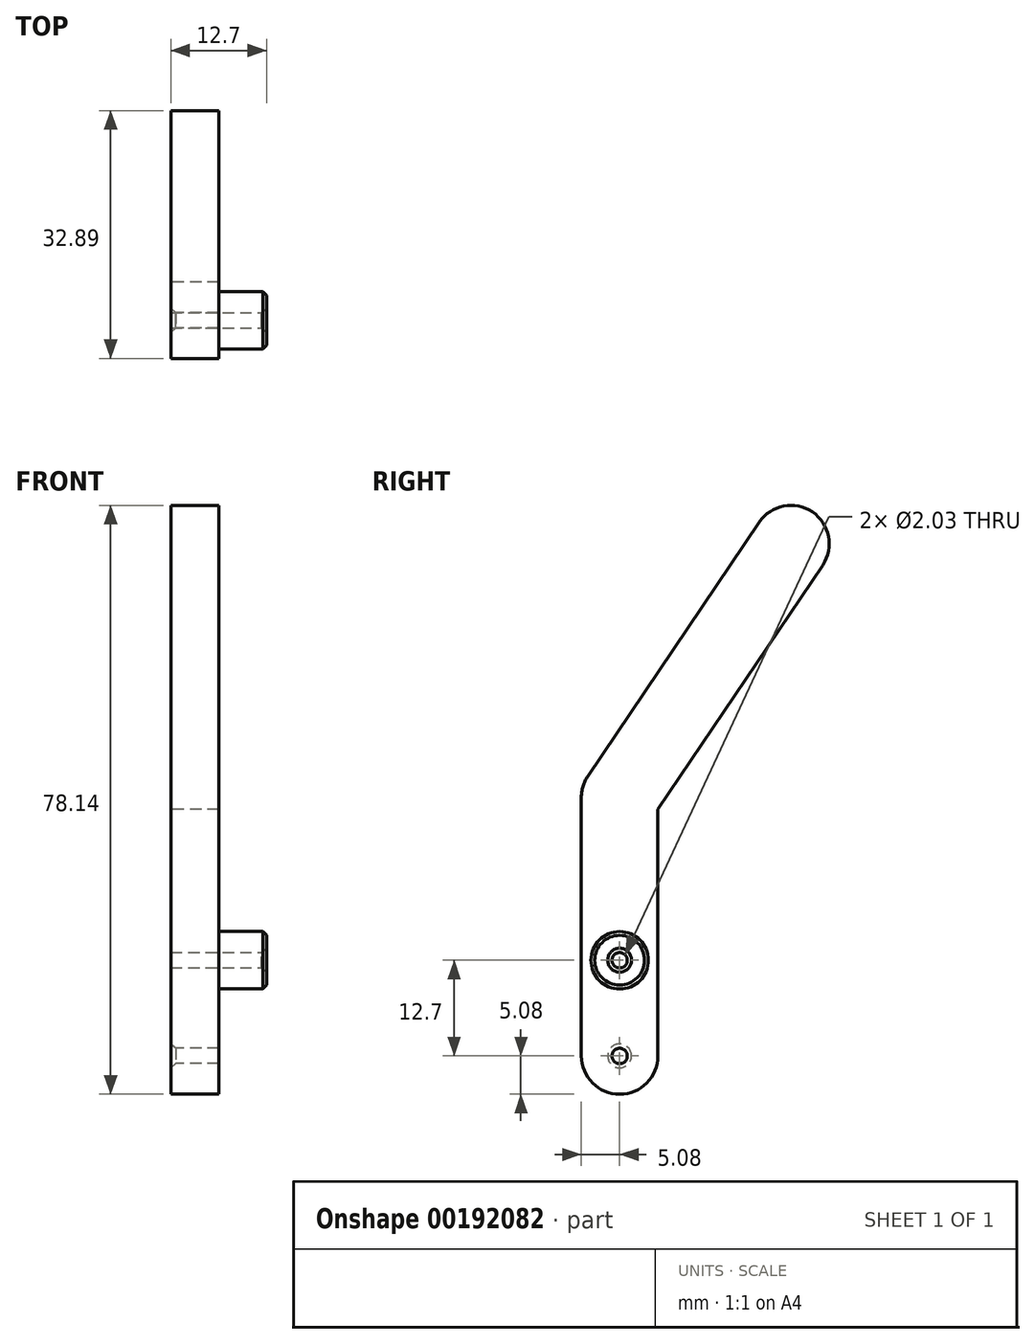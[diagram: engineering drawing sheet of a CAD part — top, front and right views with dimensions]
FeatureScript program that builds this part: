
annotation { "Feature Type Name" : "Feature", "Feature Type Description" : "" }
export const myFeature = defineFeature(function(context is Context, id is Id, definition is map)
    precondition{}
    {
        {
            var Q0;
            Q0=qCreatedBy(makeId("Right.planeOp"),FACE);
            var sketch = newSketch(context, id + "F0", { "sketchPlane" : qUnion([Q0])});
            skLineSegment(sketch, "E0", {"start": v(0, 0) * mm, "end": v(0, 12.7) * mm});
            skLineSegment(sketch, "E1", {"start": v(0, 12.7) * mm, "end": v(0, 34.3) * mm});
            skLineSegment(sketch, "E2", {"start": v(0, 34.3) * mm, "end": v(22.73, 67.98) * mm});
            skArc(sketch, "E3.0.startCap", {"start": v(5.08, 12.7) * mm, "mid": v(0, 7.62) * mm, "end": v(-5.08, 12.7) * mm});
            skArc(sketch, "E3.0.endCap", {"start": v(-5.08, 34.3) * mm, "mid": v(0, 39.37) * mm, "end": v(5.08, 34.3) * mm});
            skLineSegment(sketch, "E3.0.left", {"start": v(-5.08, 12.7) * mm, "end": v(-5.08, 34.3) * mm});
            skLineSegment(sketch, "E3.0.right", {"start": v(5.08, 12.7) * mm, "end": v(5.08, 34.3) * mm});
            skArc(sketch, "E3.1.startCap", {"start": v(4.21, 31.45) * mm, "mid": v(-2.84, 30.08) * mm, "end": v(-4.21, 37.13) * mm});
            skArc(sketch, "E3.1.endCap", {"start": v(18.51, 70.82) * mm, "mid": v(25.57, 72.2) * mm, "end": v(26.94, 65.14) * mm});
            skLineSegment(sketch, "E3.1.left", {"start": v(-4.21, 37.13) * mm, "end": v(18.51, 70.82) * mm});
            skLineSegment(sketch, "E3.1.right", {"start": v(4.21, 31.45) * mm, "end": v(26.94, 65.14) * mm});
            skArc(sketch, "E3.2.startCap", {"start": v(5.08, 0) * mm, "mid": v(0, -5.08) * mm, "end": v(-5.08, 0) * mm});
            skArc(sketch, "E3.2.endCap", {"start": v(-5.08, 12.7) * mm, "mid": v(0, 17.78) * mm, "end": v(5.08, 12.7) * mm});
            skLineSegment(sketch, "E3.2.left", {"start": v(-5.08, 0) * mm, "end": v(-5.08, 12.7) * mm});
            skLineSegment(sketch, "E3.2.right", {"start": v(5.08, 0) * mm, "end": v(5.08, 12.7) * mm});
            skSolve(sketch);
        }
        {
            var Q0;
            Q0 = qSketchRegion(id + "F0", true);
            extrude(context, id + "F1", {"entities" : qUnion([Q0]), "depth" : 6.35 * mm});
        }
        {
            var Q0;
            Q0=makeQuery(id+"F1.opExtrude","CAP_FACE",FACE,{"disambiguationData":[OSD([sQuery(id+"F0.wireOp",EDGE,"E3.0.left"),sQuery(id+"F0.wireOp",EDGE,"E3.0.right"),sQuery(id+"F0.wireOp",EDGE,"E3.1.startCap"),sQuery(id+"F0.wireOp",EDGE,"E3.1.endCap"),sQuery(id+"F0.wireOp",EDGE,"E3.1.left"),sQuery(id+"F0.wireOp",EDGE,"E3.1.right"),sQuery(id+"F0.wireOp",EDGE,"E3.2.startCap"),sQuery(id+"F0.wireOp",EDGE,"E3.2.left"),sQuery(id+"F0.wireOp",EDGE,"E3.2.right")])],"isStart":false});
            var sketch = newSketch(context, id + "F2", { "sketchPlane" : qUnion([Q0])});
            skCircle(sketch, "E4", {"center": v(0, 12.7) * mm, "radius": 3.8 * mm});
            skPoint(sketch, "E4.centerSnap0", {"position": v(-5.08, 17.14) * mm});
            skSolve(sketch);
        }
        {
            var Q0;
            Q0 = qSketchRegion(id + "F2", true);
            extrude(context, id + "F3", {"entities" : qUnion([Q0]), "operationType" : NewBodyOperationType.ADD, "depth" : 6.35 * mm});
        }
        {
            var Q0;
            Q0=makeQuery(id+"F3.opExtrude","CAP_FACE",FACE,{"disambiguationData":[OSD([sQuery(id+"F2.wireOp",EDGE,"E4")])],"isStart":false});
            var sketch = newSketch(context, id + "F4", { "sketchPlane" : qUnion([Q0])});
            skPoint(sketch, "E5", {"position": v(0, 12.7) * mm});
            skSolve(sketch);
        }
        {
            var Q0;
            Q0=sQuery(id+"F4.wireOp",VERTEX,"E5");
            var Q1;
            Q1=makeQuery(id+"F1.opExtrude","SWEPT_BODY",BODY,{"disambiguationData":[OSD([sQuery(id+"F0.wireOp",EDGE,"E3.0.left"),sQuery(id+"F0.wireOp",EDGE,"E3.0.right"),sQuery(id+"F0.wireOp",EDGE,"E3.1.startCap"),sQuery(id+"F0.wireOp",EDGE,"E3.1.endCap"),sQuery(id+"F0.wireOp",EDGE,"E3.1.left"),sQuery(id+"F0.wireOp",EDGE,"E3.1.right"),sQuery(id+"F0.wireOp",EDGE,"E3.2.startCap"),sQuery(id+"F0.wireOp",EDGE,"E3.2.left"),sQuery(id+"F0.wireOp",EDGE,"E3.2.right")])]});
            hole(context, id + "F5", {"style" : HoleStyle.C_SINK, "endStyle" : HoleEndStyle.THROUGH, "holeDiameter" : 2.03 * mm, "cSinkDiameter" : 3.17 * mm, "cSinkAngle" : 82 * degree, "locations" : qUnion([Q0]), "scope" : qUnion([Q1]), "isTappedThrough" : true});
        }
        {
            var Q0;
            Q0=sQuery(id+"F0.wireOp",VERTEX,"E3.2.startCap.center");
            var Q1;
            Q1=makeQuery(id+"F1.opExtrude","SWEPT_BODY",BODY,{"disambiguationData":[OSD([sQuery(id+"F0.wireOp",EDGE,"E3.0.left"),sQuery(id+"F0.wireOp",EDGE,"E3.0.right"),sQuery(id+"F0.wireOp",EDGE,"E3.1.startCap"),sQuery(id+"F0.wireOp",EDGE,"E3.1.endCap"),sQuery(id+"F0.wireOp",EDGE,"E3.1.left"),sQuery(id+"F0.wireOp",EDGE,"E3.1.right"),sQuery(id+"F0.wireOp",EDGE,"E3.2.startCap"),sQuery(id+"F0.wireOp",EDGE,"E3.2.left"),sQuery(id+"F0.wireOp",EDGE,"E3.2.right")])]});
            hole(context, id + "F6", {"style" : HoleStyle.C_SINK, "endStyle" : HoleEndStyle.THROUGH, "oppositeDirection" : true, "holeDiameter" : 2.03 * mm, "cSinkDiameter" : 3.17 * mm, "cSinkAngle" : 82 * degree, "locations" : qUnion([Q0]), "scope" : qUnion([Q1]), "isTappedThrough" : true});
        }
        {
            var Q0;
            Q0=makeQuery(id+"F3.opExtrude","CAP_EDGE",EDGE,{"disambiguationData":[OSD([sQuery(id+"F2.wireOp",EDGE,"E4")])],"isStart":false});
            chamfer(context, id + "F7", {"entities" : qUnion([Q0]), "width" : 0.5 * mm, "tangentPropagation" : true});
        }
    });
